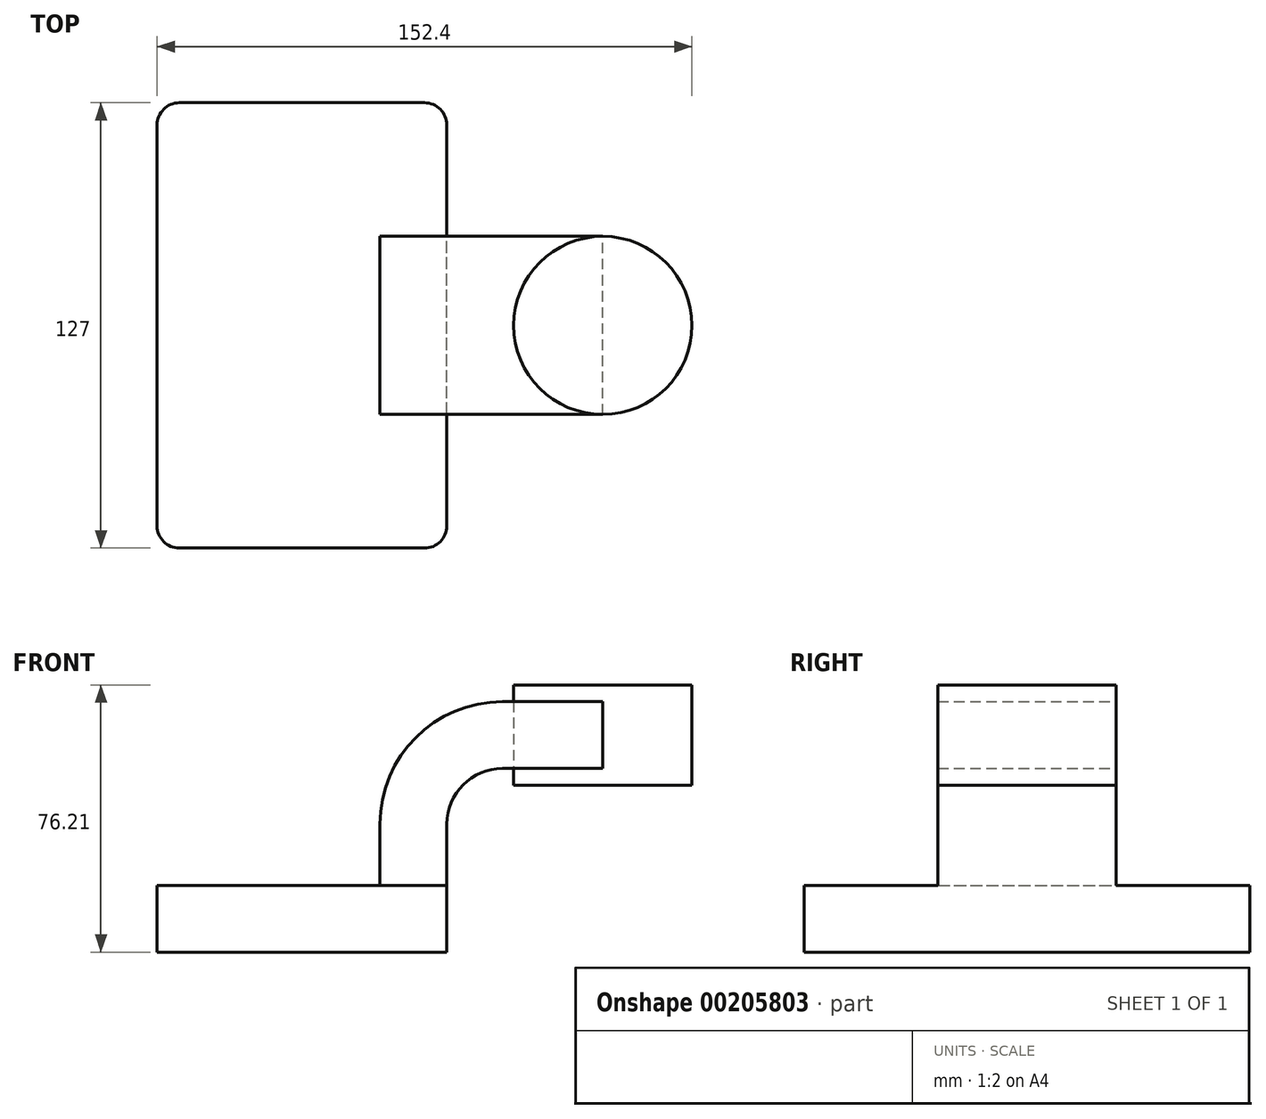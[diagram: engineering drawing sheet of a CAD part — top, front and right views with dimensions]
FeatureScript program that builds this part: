
annotation { "Feature Type Name" : "Feature", "Feature Type Description" : "" }
export const myFeature = defineFeature(function(context is Context, id is Id, definition is map)
    precondition{}
    {
        {
            var Q0;
            Q0=qCreatedBy(makeId("Front.planeOp"),FACE);
            var sketch = newSketch(context, id + "F0", { "sketchPlane" : qUnion([Q0])});
            skLineSegment(sketch, "E0.bottom", {"start": v(-41.28, -9.53) * mm, "end": v(41.28, -9.53) * mm});
            skLineSegment(sketch, "E0.top", {"start": v(-41.28, 9.52) * mm, "end": v(41.28, 9.52) * mm});
            skLineSegment(sketch, "E0.left", {"start": v(-41.28, -9.53) * mm, "end": v(-41.28, 9.53) * mm});
            skLineSegment(sketch, "E0.right", {"start": v(41.28, -9.53) * mm, "end": v(41.28, 9.52) * mm});
            skPoint(sketch, "E0.middle", {"position": v(0, 0) * mm});
            skLineSegment(sketch, "E1.bottom", {"start": v(111.12, 38.1) * mm, "end": v(60.32, 38.1) * mm});
            skLineSegment(sketch, "E1.top", {"start": v(111.12, 66.68) * mm, "end": v(60.32, 66.68) * mm});
            skLineSegment(sketch, "E1.left", {"start": v(111.12, 38.1) * mm, "end": v(111.12, 66.67) * mm});
            skLineSegment(sketch, "E1.right", {"start": v(60.32, 38.1) * mm, "end": v(60.33, 66.68) * mm});
            skPoint(sketch, "E1.middle", {"position": v(85.72, 52.39) * mm});
            skLineSegment(sketch, "E2", {"start": v(41.28, 9.52) * mm, "end": v(41.28, 26.97) * mm});
            skArc(sketch, "E3", {"start": v(41.27, 26.97) * mm, "mid": v(45.92, 38.2) * mm, "end": v(57.15, 42.85) * mm});
            skLineSegment(sketch, "E4", {"start": v(57.15, 42.85) * mm, "end": v(94.56, 42.85) * mm});
            skLineSegment(sketch, "E5.0", {"start": v(57.15, 61.9) * mm, "end": v(94.56, 61.9) * mm});
            skArc(sketch, "E5.1", {"start": v(22.22, 26.97) * mm, "mid": v(32.45, 51.67) * mm, "end": v(57.15, 61.9) * mm});
            skLineSegment(sketch, "E5.2", {"start": v(22.22, 9.52) * mm, "end": v(22.22, 26.97) * mm});
            skLineSegment(sketch, "E6", {"start": v(85.72, 38.1) * mm, "end": v(85.72, 66.68) * mm});
            skFitSpline(sketch, "E7", {"points": [v(-41.28, 9.53) * mm, v(60.32, 66.67) * mm], "startDerivative": vector(54.63, 108.5) * mm, "endDerivative": vector(149.44, 6.02) * mm});
            skSolve(sketch);
        }
        {
            var Q0;
            {var subQ1=sQuery(id+"F0.wireOp",EDGE,"E2");Q0=makeQuery(id+"F0.imprint","IMPRINT",FACE,{"disambiguationData":[TD([[makeQuery(id+"F0.imprint","IMPRINT",EDGE,{"derivedFrom":subQ1}),1.0]])]});}
            var Q1;
            {var subQ0=sQuery(id+"F0.wireOp",EDGE,"E4");var subQ1=sQuery(id+"F0.wireOp",EDGE,"E1.right");var subQ2=makeQuery(id+"F0.imprint","INTERSECT",VERTEX,{"derivedFrom":[subQ1,subQ0]});Q1=makeQuery(id+"F0.imprint","IMPRINT",FACE,{"disambiguationData":[TD([[makeQuery(id+"F0.imprint","IMPRINT",EDGE,{"disambiguationData":[TD([[subQ2,-1.0]])],"derivedFrom":subQ1}),-1.0]])]});}
            extrude(context, id + "F1", {"entities" : qUnion([Q0, Q1]), "endBound" : BoundingType.SYMMETRIC, "depth" : 50.8 * mm});
        }
        {
            var Q0;
            Q0=makeQuery(id+"F0.imprint","IMPRINT",FACE,{"disambiguationData":[TD([[makeQuery(id+"F0.imprint","IMPRINT",EDGE,{"derivedFrom":sQuery(id+"F0.wireOp",EDGE,"E0.bottom")}),1.0]])]});
            extrude(context, id + "F2", {"entities" : qUnion([Q0]), "operationType" : NewBodyOperationType.ADD, "endBound" : BoundingType.SYMMETRIC, "depth" : 127 * mm});
        }
        {
            var Q0;
            {var subQ0=sQuery(id+"F0.wireOp",EDGE,"E5.1");Q0=makeQuery(id+"F0.imprint","IMPRINT",FACE,{"disambiguationData":[TD([[makeQuery(id+"F0.imprint","IMPRINT",EDGE,{"derivedFrom":subQ0}),1.0]])]});}
            extrude(context, id + "F3", {"entities" : qUnion([Q0]), "operationType" : NewBodyOperationType.ADD, "endBound" : BoundingType.SYMMETRIC, "depth" : 15.88 * mm});
        }
        {
            var Q0;
            {var subQ0=sQuery(id+"F0.wireOp",EDGE,"E1.left");Q0=makeQuery(id+"F0.imprint","IMPRINT",FACE,{"disambiguationData":[TD([[makeQuery(id+"F0.imprint","IMPRINT",EDGE,{"derivedFrom":subQ0}),1.0]])]});}
            var Q1;
            Q1=sQuery(id+"F0.wireOp",EDGE,"E6");
            revolve(context, id + "F4", {"entities" : qUnion([Q0]), "axis" : qUnion([Q1]), "revolveType" : RevolveType.FULL});
        }
        {
            var Q0;
            Q0=makeQuery(id+"F2.opExtrude","CAP_EDGE",EDGE,{"disambiguationData":[OSD([sQuery(id+"F0.wireOp",EDGE,"E0.left")])],"isStart":false});
            var Q1;
            Q1=makeQuery(id+"F2.opExtrude","CAP_EDGE",EDGE,{"disambiguationData":[OSD([sQuery(id+"F0.wireOp",EDGE,"E0.right")])],"isStart":false});
            var Q2;
            Q2=makeQuery(id+"F2.opExtrude","CAP_EDGE",EDGE,{"disambiguationData":[OSD([sQuery(id+"F0.wireOp",EDGE,"E0.right")])],"isStart":true});
            var Q3;
            Q3=makeQuery(id+"F2.opExtrude","CAP_EDGE",EDGE,{"disambiguationData":[OSD([sQuery(id+"F0.wireOp",EDGE,"E0.left")])],"isStart":true});
            fillet(context, id + "F5", {"entities" : qUnion([Q0, Q1, Q2, Q3]), "radius" : 6.35 * mm, "tangentPropagation" : true, "allowEdgeOverflow" : false});
        }
    });
